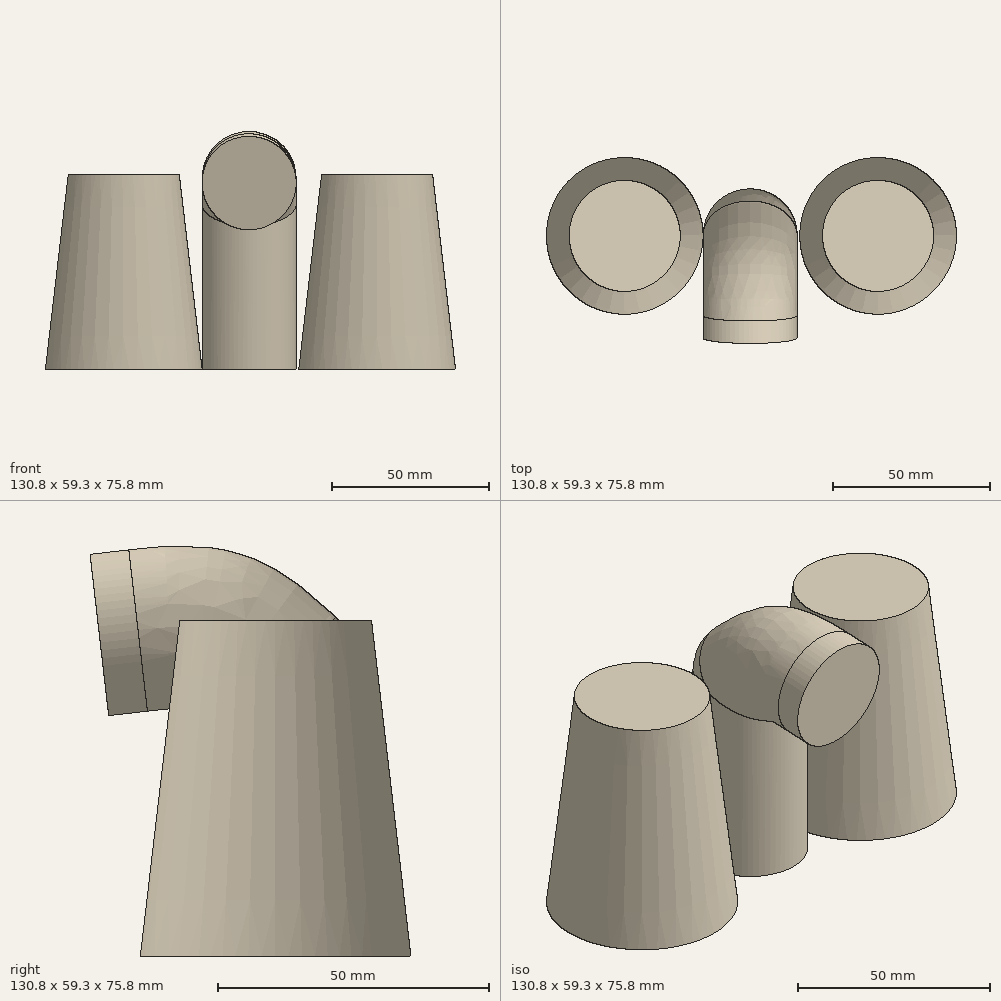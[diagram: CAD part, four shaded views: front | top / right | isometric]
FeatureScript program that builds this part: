
annotation { "Feature Type Name" : "Feature", "Feature Type Description" : "" }
export const myFeature = defineFeature(function(context is Context, id is Id, definition is map)
    precondition{}
    {
        {
            var Q0;
            Q0=qCreatedBy(makeId("Top.planeOp"),FACE);
            var sketch = newSketch(context, id + "F0", { "sketchPlane" : qUnion([Q0])});
            skCircle(sketch, "E0", {"center": v(-43.01, 0) * mm, "radius": 25 * mm});
            skCircle(sketch, "E1", {"center": v(37.79, 0) * mm, "radius": 25 * mm});
            skLineSegment(sketch, "E2", {"start": v(-43.01, 0) * mm, "end": v(-3.01, 0) * mm});
            skCircle(sketch, "E3", {"center": v(-3.01, 0) * mm, "radius": 15 * mm});
            skSolve(sketch);
        }
        {
            var Q0;
            Q0=makeQuery(id+"F0.imprint","IMPRINT",FACE,{"disambiguationData":[TD([[makeQuery(id+"F0.imprint","IMPRINT",EDGE,{"derivedFrom":sQuery(id+"F0.wireOp",EDGE,"E0")}),1.0]])]});
            var Q1;
            Q1=makeQuery(id+"F0.imprint","IMPRINT",FACE,{"disambiguationData":[TD([[makeQuery(id+"F0.imprint","IMPRINT",EDGE,{"derivedFrom":sQuery(id+"F0.wireOp",EDGE,"E1")}),1.0]])]});
            extrude(context, id + "F1", {"entities" : qUnion([Q0, Q1]), "depth" : 62 * mm, "offsetDistance" : 25 * mm, "hasDraft" : true, "draftAngle" : 6.7 * degree, "draftPullDirection" : true});
        }
        {
            var Q0;
            Q0=makeQuery(id+"F0.imprint","IMPRINT",FACE,{"disambiguationData":[TD([[makeQuery(id+"F0.imprint","IMPRINT",EDGE,{"derivedFrom":sQuery(id+"F0.wireOp",EDGE,"E3")}),1.0]])]});
            extrude(context, id + "F2", {"entities" : qUnion([Q0]), "depth" : 42.3 * mm, "offsetDistance" : 25 * mm});
        }
        {
            var Q0;
            Q0=qCreatedBy(makeId("Right.planeOp"),FACE);
            var sketch = newSketch(context, id + "F3", { "sketchPlane" : qUnion([Q0])});
            skFitSpline(sketch, "E4", {"points": [v(0, 42.7) * mm, v(0, 52.52) * mm], "startDerivative": vector(0, 9.8) * mm, "endDerivative": vector(0, 9.8) * mm});
            skLineSegment(sketch, "E5", {"start": v(0, 52.52) * mm, "end": v(0, 42.7) * mm});
            skFitSpline(sketch, "E6", {"points": [v(0, 52.52) * mm, v(-10.79, 59.98) * mm, v(-25.82, 60.16) * mm], "startDerivative": vector(-20.7, 19.1) * mm, "endDerivative": vector(-30.81, -3.56) * mm});
            skSolve(sketch);
        }
        {
            var Q0;
            Q0=makeQuery(id+"F2.opExtrude","CAP_FACE",FACE,{"disambiguationData":[OSD([sQuery(id+"F0.wireOp",EDGE,"E3")])],"isStart":false});
            var Q1;
            Q1=sQuery(id+"F3.wireOp",EDGE,"E6");
            var Q2;
            Q2=sQuery(id+"F3.wireOp",EDGE,"E5");
            sweep(context, id + "F4", {"operationType" : NewBodyOperationType.ADD, "profiles" : qUnion([Q0]), "path" : qUnion([Q1, Q2])});
        }
        {
            var Q0;
            Q0=makeQuery(id+"F4.opSweep","CAP_FACE",FACE,{"disambiguationData":[OSD([sQuery(id+"F0.wireOp",EDGE,"E3"),sQuery(id+"F3.wireOp",VERTEX,"E6.end")])],"isStart":false});
            extrude(context, id + "F5", {"entities" : qUnion([Q0]), "operationType" : NewBodyOperationType.ADD, "depth" : 7.2 * mm, "offsetDistance" : 25 * mm});
        }
        {
            var Q0;
            Q0=makeQuery(id+"F4.opSweep","MID_CAP_EDGE",EDGE,{"disambiguationData":[OSD([sQuery(id+"F0.wireOp",EDGE,"E3"),sQuery(id+"F3.wireOp",VERTEX,"E5.start")]),OD(1.0)],"capPos":1.0});
            fillet(context, id + "F6", {"entities" : qUnion([Q0]), "radius" : 12 * mm, "tangentPropagation" : true, "allowEdgeOverflow" : false});
        }
    });
